SOLIDWORKS PART (.sldprt)
format: sldprt  version: not decoded by parser v0  size: 99,328 bytes
history: native  units: mm
features: sketch x3, cut_extrude x2, material x1, extrude x1 (+11 scaffold rows collapsed)
feature tree (18):
  scaffold x11  (default folders/planes/origin — collapsed)
  material  "Material <not specified>"
  sketch  "Sketch1"  dims[D1=80.0mm D2=120.0mm]
  extrude  "Boss-Extrude1"  Depth=10mm
  sketch  "Sketch2"  dims[D1=3.5mm D5=3.5mm D2=7.5mm D3=17.0mm D4=17.0mm D6=66.5mm]
  cut_extrude  "Cut-Extrude1"  [1 undecoded]
  sketch  "Sketch3"  dims[D1=6.5mm D2=6.5mm]
  cut_extrude  "Cut-Extrude2"  Depth=5mm
decode coverage: 5 of 6 modeling features carry decoded parameters
note: 1 parameter value undecoded
note: suppression state not decoded; provenance and decode notes live in map.json
